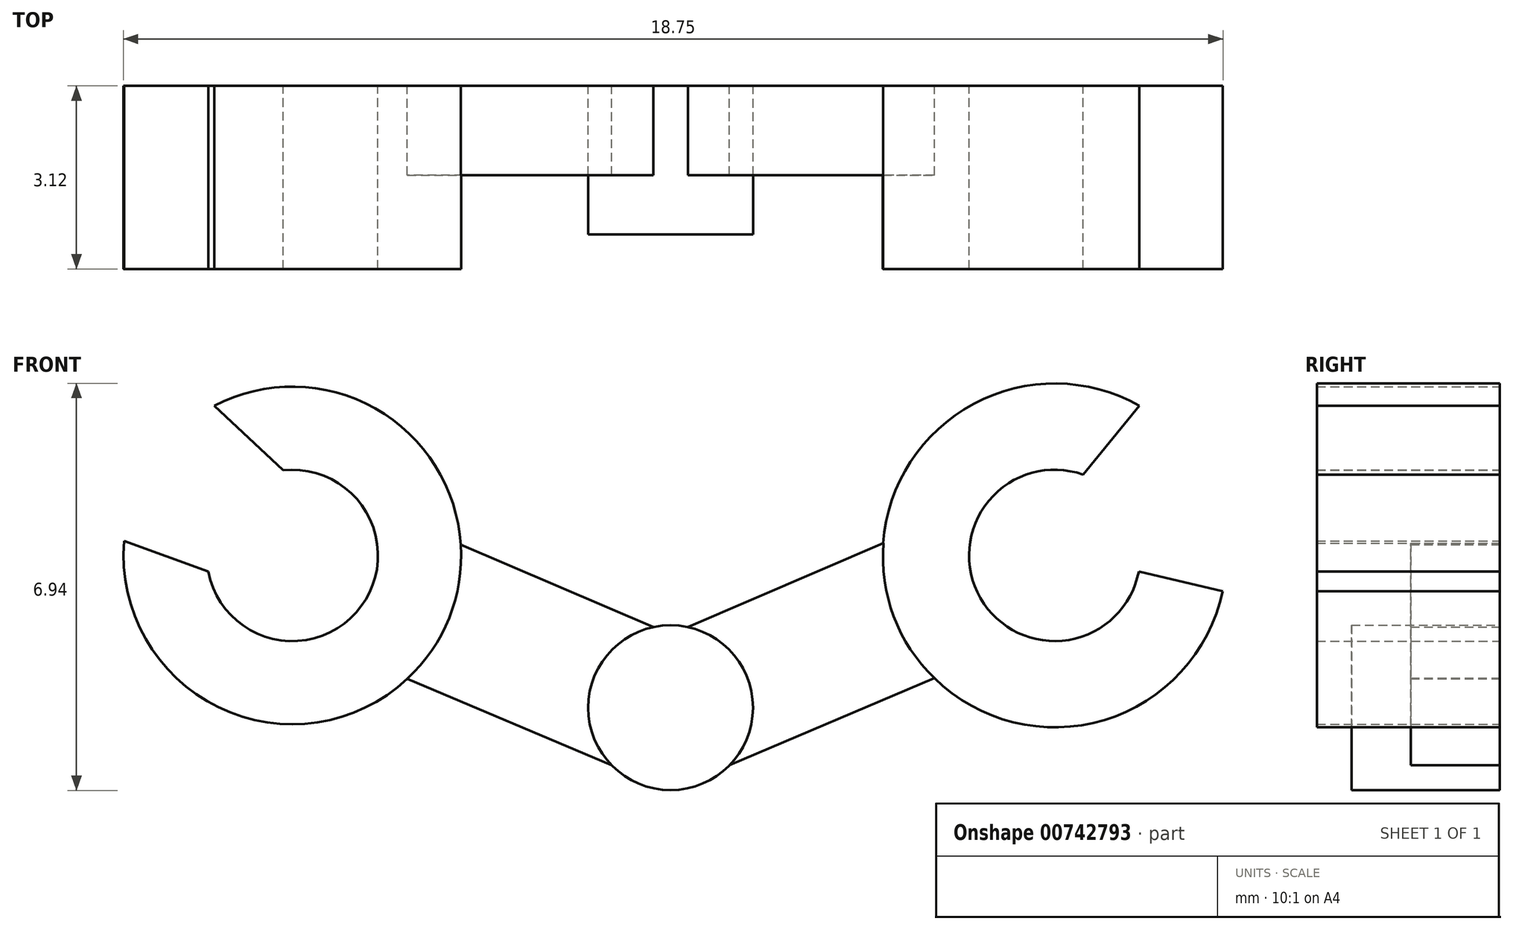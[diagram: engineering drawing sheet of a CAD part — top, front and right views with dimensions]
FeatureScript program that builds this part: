
annotation { "Feature Type Name" : "Feature", "Feature Type Description" : "" }
export const myFeature = defineFeature(function(context is Context, id is Id, definition is map)
    precondition{}
    {
        {
            var Q0;
            Q0=qCreatedBy(makeId("Front.planeOp"),FACE);
            var sketch = newSketch(context, id + "F0", { "sketchPlane" : qUnion([Q0])});
            skCircle(sketch, "E0", {"center": v(0, 0) * mm, "radius": 1.4 * mm});
            skLineSegment(sketch, "E1", {"start": v(-0.3, 1.37) * mm, "end": v(-3.63, 2.8) * mm});
            skLineSegment(sketch, "E2", {"start": v(-1, -0.98) * mm, "end": v(-4.54, 0.51) * mm});
            skLineSegment(sketch, "E3", {"start": v(0.3, 1.37) * mm, "end": v(3.63, 2.8) * mm});
            skLineSegment(sketch, "E4", {"start": v(4.5, 0.5) * mm, "end": v(1, -0.98) * mm});
            skArc(sketch, "E5", {"start": v(-7.88, 2.32) * mm, "mid": v(-5.28, 1.73) * mm, "end": v(-6.6, 4.05) * mm});
            skArc(sketch, "E6", {"start": v(-9.32, 2.84) * mm, "mid": v(-7.7, 0) * mm, "end": v(-4.49, 0.5) * mm});
            skLineSegment(sketch, "E7", {"start": v(-9.32, 2.84) * mm, "end": v(-7.88, 2.32) * mm});
            skLineSegment(sketch, "E8", {"start": v(-7.78, 5.15) * mm, "end": v(-6.6, 4.05) * mm});
            skPoint(sketch, "E9.start.orphan", {"position": v(-4.09, 1.66) * mm});
            skArc(sketch, "E10.trimOffspring", {"start": v(-3.58, 2.78) * mm, "mid": v(-5.04, 5.1) * mm, "end": v(-7.78, 5.15) * mm});
            skLineSegment(sketch, "E11", {"start": v(4.12, 1.68) * mm, "end": v(5.54, 2.29) * mm});
            skPoint(sketch, "E12.center.orphan", {"position": v(6.97, 2.6) * mm});
            skArc(sketch, "E13", {"start": v(7.03, 3.97) * mm, "mid": v(5.28, 1.87) * mm, "end": v(7.98, 2.32) * mm});
            skArc(sketch, "E14", {"start": v(4.5, 0.5) * mm, "mid": v(7.4, -0.21) * mm, "end": v(9.42, 1.98) * mm});
            skPoint(sketch, "E15.endSnap0", {"position": v(4.83, 1.98) * mm});
            skLineSegment(sketch, "E16", {"start": v(7.98, 2.32) * mm, "end": v(9.42, 1.98) * mm});
            skLineSegment(sketch, "E17", {"start": v(8, 5.15) * mm, "end": v(7.03, 3.97) * mm});
            skPoint(sketch, "E18.start.orphan", {"position": v(6.4, 4.05) * mm});
            skArc(sketch, "E19.trimOffspring", {"start": v(8, 5.15) * mm, "mid": v(5.17, 5.18) * mm, "end": v(3.63, 2.8) * mm});
            skArc(sketch, "E20", {"start": v(-4.49, 0.5) * mm, "mid": v(-3.78, 1.53) * mm, "end": v(-3.58, 2.78) * mm});
            skPoint(sketch, "E21.orphan", {"position": v(4.6, 0.55) * mm});
            skArc(sketch, "E22", {"start": v(3.63, 2.8) * mm, "mid": v(3.8, 1.56) * mm, "end": v(4.5, 0.5) * mm});
            skSolve(sketch);
        }
        {
            var Q0;
            Q0=makeQuery(id+"F0.imprint","IMPRINT",FACE,{"disambiguationData":[TD([[makeQuery(id+"F0.imprint","IMPRINT",EDGE,{"derivedFrom":sQuery(id+"F0.wireOp",EDGE,"E14")}),1.0]])]});
            var Q1;
            Q1=makeQuery(id+"F0.imprint","IMPRINT",FACE,{"disambiguationData":[TD([[makeQuery(id+"F0.imprint","IMPRINT",EDGE,{"derivedFrom":sQuery(id+"F0.wireOp",EDGE,"E5")}),-1.0]])]});
            extrude(context, id + "F1", {"entities" : qUnion([Q0, Q1]), "depth" : 3.12 * mm, "offsetDistance" : 25 * mm});
        }
        {
            var Q0;
            {var subQ0=sQuery(id+"F0.wireOp",EDGE,"E0");var subQ1=makeQuery(id+"F0.imprint","INTERSECT",VERTEX,{"derivedFrom":[subQ0,sQuery(id+"F0.wireOp",EDGE,"E1")]});Q0=makeQuery(id+"F0.imprint","IMPRINT",FACE,{"disambiguationData":[TD([[makeQuery(id+"F0.imprint","IMPRINT",EDGE,{"disambiguationData":[TD([[subQ1,1.0]])],"derivedFrom":subQ0}),1.0]])]});}
            extrude(context, id + "F2", {"entities" : qUnion([Q0]), "depth" : 2.53 * mm, "offsetDistance" : 25 * mm});
        }
        {
            var Q0;
            {var subQ5=sQuery(id+"F0.wireOp",EDGE,"E20");Q0=makeQuery(id+"F0.imprint","IMPRINT",FACE,{"disambiguationData":[TD([[makeQuery(id+"F0.imprint","IMPRINT",EDGE,{"derivedFrom":subQ5}),-1.0]])]});}
            var Q1;
            {var subQ5=sQuery(id+"F0.wireOp",EDGE,"E4");Q1=makeQuery(id+"F0.imprint","IMPRINT",FACE,{"disambiguationData":[TD([[makeQuery(id+"F0.imprint","IMPRINT",EDGE,{"derivedFrom":subQ5}),-1.0]])]});}
            extrude(context, id + "F3", {"entities" : qUnion([Q0, Q1]), "depth" : 1.52 * mm, "offsetDistance" : 25 * mm});
        }
    });
